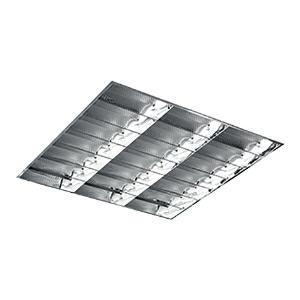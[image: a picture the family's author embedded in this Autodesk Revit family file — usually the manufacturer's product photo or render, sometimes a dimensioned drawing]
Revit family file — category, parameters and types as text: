
# Revit family: 3f_filippi_-_l_320_2mg_3f_filippi_-_22724_-_l_323x10w-940_led_dali_2mg_596x596
name_source: partatom
category: Lighting Fixtures
units: mm (PartAtom-declared; Revit-internal decimal feet)

## family parameters
Cut with Voids When Loaded = No
Host = Face
Light Source = No
Part Type = Normal
Room Calculation Point = No
Round Connector Dimension = Use Diameter
Shared = No

## types (1)
- 3F Filippi - L 320 2MG (1 x LED, 3323 lm, 34 W, 4000 K)
    Apparent Load = 34 VA
    Approval mark = ENEC
    CIE Flux Codes = 71 98 100 100 100
    Color Rendering = 90
    Color Temperature = 4000 K
    Control Gear = Electronic transformer
    Default Elevation = 1800 mm
    Description = ILLUMINOTECHNICAL
Luminous efficiency 100% (DLOR 100%, ULOR 0%).
Initial luminous flux of the luminaire 3323 lm.
Direct symmetric distribution.
Installation Interdistance Transv.D = 1.27 x hu - Long.D = 1.17 x hu.
Average luminance <1000 cd/m² for radial angles >65°.
Tabular UGR (CIE 117 - 4H-8H; S=0.25H; 70/50/20): RUG 14.2 - 14.6.
Beam angle: 87° - 88°.
Luminous efficacy 98 lm/W.
Lifetime (L93/B10): 30000 h. (tq+25°C)
Lifetime (L90/B10): 50000 h. (tq+25°C)
Lifetime (L85/B10): 80000 h. (tq+25°C)
Lifetime (L80/B10): 100000 h. (tq+25°C)
Sudden decreased luminous flux after 50000 hours: 0% (C0).
Photobiological safety in compliance with IEC/TR 62778: RG0 risk exempt, (IEC 62471).
In compliance with IEC/EN 62722-2-1 - IEC/EN 62717 standards.

SOURCE
3 linear LED modules 10W/940.
Energy efficiency class (UE 2019/2020 - UE 2019/2015): E.
CIE 13.3 Colour rendering index: CRI >90 (R9 >50%).
IES TM-30 Fidelity Index: Rf = 92 Rg = 101.
CCT nominal colour temperature 4000 K.
Colour initial tolerance (MacAdam): SDCM 2.

MECHANICAL
Housing in hot-galvanised steel, painted in white polyester.
2MG parabolic louvre, high efficiency, in specular aluminium with superficial titanium-magnesium treatment, non-iridescent, with transverse blades closed at the top.
Prismatic flat diffusers in transparent methacrylate (PMMA), multilenticular, anti-glare, prismatic outer surface, positioned above the louvre blades.
Film protective against dust and finger marks, adhesive, attached to louvre.
Luminaire with limited surface temperature. - D - (EN 60598-2-24)
Dimensions: 596x596 mm, height 80 mm. Weight 3.685 kg.
IP20 protection degree.
Mechanical strength to impacts IK02 (0.2 joule).
Glow-wire test resistance 650°C.

ELECTRICAL
Halogen Free DALI-2 DATI (Parts 251, 252, 253), PUSH-DIM, electronic wiring 230V-50/60Hz, power factor 0.95 at full load, THD <25%, constant output current, SELV, class I, 1 driver, 1 DALI addresse.
Power of the luminaire 34 W.
CE - IEC 60598-1 - EN 60598-1.
SAFE FLICKER: PstLM=<1 and SVM=<0.4 (IEC TR 61547-1 and IEC TR 63158), to ensure a more comfortable and safe light.
Luminaire compliant with EN 60598-2-22 for power supply from a centralised emergency system CPSS (Central Power Supply System), not incorporated in the luminaire - high risk areas excluded. The default power and flux are 100% in AC and 15% in DC.
Ambient temperature from 0°C to +25°C.
Temperature class T6 max 85°C.
Relative humidity UR: <85%.

INSTALLATION
Lay-in recessed fitting.
On request: pull-up recessed fitting with brackets.
False ceiling carving: 580x580 mm.
All accessories dedicated to this product are available on the Catalog and on our website www.3F-Filippi.com.

APPLICATIONS
In environments with VDTs, managerial offices and staterooms, public offices and schools.

LIGHT MANAGEMENT
Recommended minimum setting: 10%.
The luminaire, equipped with (DALI-2 DATI) driver, can be controlled manually with 3F Easy Dim technology or automatically/manually with wired or wireless DALI/D2D control systems.
The D2D driver guarantees interoperability with other devices with the same certification by making the following information available:
Device Data (Part 251), Energy Report (Part 252), Diagnosis & Maintenance (Part 253).
In electrical systems without a regulation system (manual or automatic) and DALI bus, a suitable jumper must be made on the DA-DA terminals of the appliance.

WARNING
Luminaire designed for disposal/recycling at end-of-life.
Replaceable (LED only) light source by a professional. Replaceable control gear by a professional.
    Height = 0 mm  [stored 0 ft]
    Lamp = 1 x LED
    Lamp Light Flux = 3323 lm
    Lamp Power = 34 W
    Lamp count = 1
    Length = 596 mm
    Lifetime = 50000 h
    Luminous efficacy = 98 lm/W
    Manufacturer = 3F Filippi
    ModVariant = No
    Model = 3F Filippi - 22724 - L 323x10W-940 LED DALI 2MG 596x596
    Mounting Place = Ceiling
    Mounting Type = Recessed
    Number of Poles = 1
    OnlyDefault = Yes
    Power Factor = 1
    Product Name = 3F Filippi - L 320 2MG
    Product group = recessed luminaire
    ProductGroupID = 4
    Protection Class = Protection class I
    Protection Degree = IP 20
    RLX_Detail_Level = 1
    RLX_Emergency_Light_Flux = 0 lm
    RLX_Emergency_Type = 0
    RLX_Emergency_Type_DB = No
    RlxData = <blob elided: 52509 chars, md5=7dd1f7f9>
    Socket = socket
    Standby Power = 0 W
    System Light Flux = 3323 lm
    System Power = 34 W
    Type Comments = Product without accessories
    Type Image = 3ffilippi_l_320_led_2mg.jpg
    URL = http://relux.com
    VarID = ---
    Voltage = 0 V
    Weight = 0.00 kg
    Width = 596 mm

note: [stored X ft] marks values corroborated as IEEE doubles in the binary element streams (Revit-internal decimal feet)

## geometry (parser evidence)
native form markers: Blend x4, Sweep x11
no freeform markers — native parametric forms only
